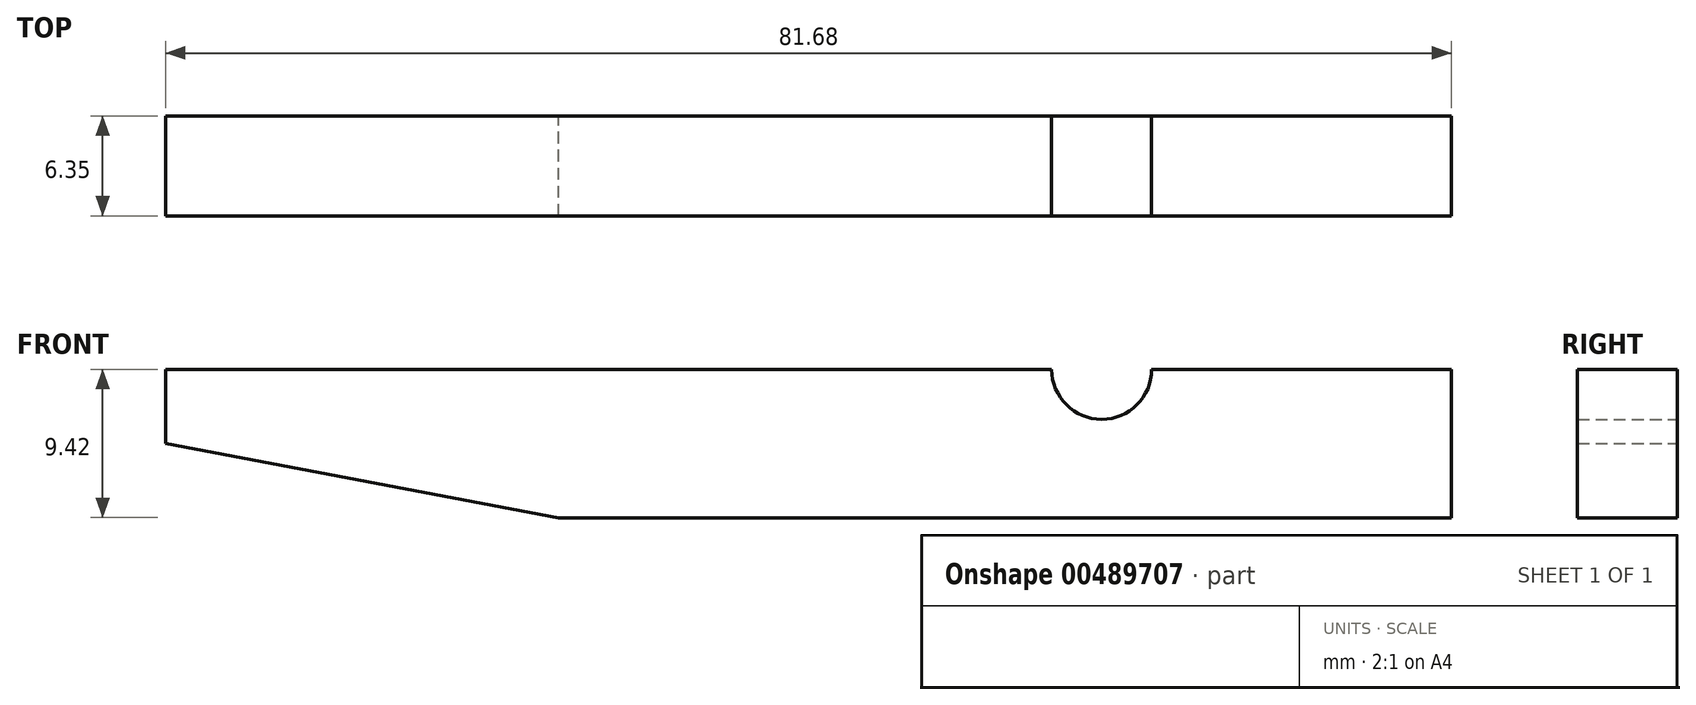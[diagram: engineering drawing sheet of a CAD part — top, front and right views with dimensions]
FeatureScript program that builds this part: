
annotation { "Feature Type Name" : "Feature", "Feature Type Description" : "" }
export const myFeature = defineFeature(function(context is Context, id is Id, definition is map)
    precondition{}
    {
        {
            var Q0;
            Q0=qCreatedBy(makeId("Front.planeOp"),FACE);
            var sketch = newSketch(context, id + "F0", { "sketchPlane" : qUnion([Q0])});
            skLineSegment(sketch, "E0.bottom", {"start": v(-40.84, 4.71) * mm, "end": v(15.44, 4.71) * mm});
            skLineSegment(sketch, "E0.top", {"start": v(-15.89, -4.71) * mm, "end": v(40.84, -4.71) * mm});
            skLineSegment(sketch, "E0.left", {"start": v(-40.84, 4.71) * mm, "end": v(-40.84, 0) * mm});
            skLineSegment(sketch, "E0.right", {"start": v(40.84, 4.71) * mm, "end": v(40.84, -4.71) * mm});
            skPoint(sketch, "E0.middle", {"position": v(0, 0) * mm});
            skArc(sketch, "E1", {"start": v(15.44, 4.71) * mm, "mid": v(18.62, 1.54) * mm, "end": v(21.8, 4.71) * mm});
            skPoint(sketch, "E2.start.orphan", {"position": v(40.84, 10.45) * mm});
            skLineSegment(sketch, "E3.trimOffspring", {"start": v(21.8, 4.71) * mm, "end": v(40.84, 4.71) * mm});
            skLineSegment(sketch, "E4", {"start": v(-40.84, 0) * mm, "end": v(-15.89, -4.71) * mm});
            skPoint(sketch, "E5.orphan", {"position": v(-40.84, -4.71) * mm});
            skSolve(sketch);
        }
        {
            var Q0;
            Q0 = qSketchRegion(id + "F0", true);
            extrude(context, id + "F1", {"entities" : qUnion([Q0]), "depth" : 6.35 * mm});
        }
    });
